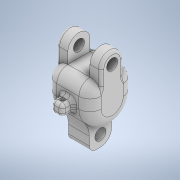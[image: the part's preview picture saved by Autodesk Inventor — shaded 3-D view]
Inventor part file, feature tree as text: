
AUTODESK INVENTOR PART (.ipt)
format: ipt  version: 2022 (Build 260153000, 153)  size: 421,888 bytes
history: native  units: mm
features: fillet x11, extrude x7, sketch x7
ambient origin geometry x8: Origin, YZ Plane, XZ Plane, XY Plane, X Axis, Y Axis, Z Axis, Center Point
bodies: Solide1 (feature_tree)
feature tree (25):
  extrude  "Extrusion1"  Depth=20.0mm
  extrude  "Extrusion2"  Depth=20.0mm
  extrude  "Extrusion3"  Depth=20.0mm TaperAngle=0.0deg
  fillet  "Congé1"  Radius=10.0mm
  fillet  "Congé2"  Radius=10.0mm
  extrude  "Extrusion4"  Depth=20.0mm TaperAngle=0.0deg
  extrude  "Extrusion5"  Depth=5.0mm
  fillet  "Congé4"  Radius=20.0mm
  fillet  "Congé5"  Radius=5.0mm
  fillet  "Congé6"  Radius=10.0mm
  fillet  "Congé7"  Radius=20.0mm
  fillet  "Congé8"  Radius=10.0mm
  fillet  "Congé9"  [1 undecoded]
  fillet  "Congé10"  Radius=10.0mm
  extrude  "Extrusion6"  Depth=5.0mm
  extrude  "Extrusion7"  Depth=43.5mm TaperAngle=0.0deg
  fillet  "Congé11"  Radius=10.0mm
  fillet  "Congé12"  Radius=5.0mm
  sketch  "Esquisse1"
  sketch  "Esquisse3"
  sketch  "Esquisse4"
  sketch  "Esquisse7"
  sketch  "Esquisse8"
  sketch  "Esquisse10"
  sketch  "Esquisse11"
note: 1 required parameter value undecoded (feature->parameter linkage not recoverable at this tier; creation-order binding heuristic only, values carry confidence <= 0.55)
